# Revit family: Б406 исп.2_RV17_LOD400 (05.11.23)
name_source: partatom
category: Электрооборудование
revit_build: Autodesk Revit 2017 (Build: 20170118_1100(x64)
units: mm (PartAtom-declared; Revit-internal decimal feet)

## family parameters
Всегда вертикально = Нет
Конфигурация панели = Два столбца, слева направо
На основе рабочей плоскости = Да
Общий = Нет
При загрузке вырезать с полостями = Нет
Размер круглого соединителя = Использовать диаметр
Тип детали = Щит
Точка расчета площади = Нет

## types (1)
- Б406
    ADSK_URL страницы изделия = https://stilsoft.ru
    ADSK_Единица измерения = шт.
    ADSK_Завод-изготовитель = ООО «Основа Безопасности»
    ADSK_Количество = 1
    ADSK_Марка = CТАЕ.431295.108-01
    ADSK_Масса = 0.5
    ADSK_Наименование = Конвертер интерфейсов Б406
    ADSK_Размер_Высота = 35 мм
    ADSK_Размер_Глубина = 92 мм
    ADSK_Размер_Длина = 140 мм
    d_короба = 20 мм
    Диапазон рабочих температур, °С = от - 40 до + 50
    Длина линии RS-485, до, м = 1200
    Количество каналов, шт = 2
    Конфигурирование = Веб-интерфейс
    Максимальное количество конвертеров подключенных к одному серверу, шт. = до 1024
    Напряжение = 12
    Отметка по умолчанию = 1219 мм
    Потребляемый ток не более, А = 0 А
    Стандарт интерфейса связи = Ethernet
    Управление устройствами с интерфейсом RS-232 или RS-485 на скорости, Бит/с = до 115200
